# Revit family: Roof_Top_AHU-Systemair-ERV_Series
name_source: partatom
category: Mechanical Equipment
revit_build: Autodesk Revit MEP 2013 (Build: 20121003_2115(x64)
units: mm (PartAtom-declared; Revit-internal decimal feet)

## types (1)
- ERV 1300RT-EC
    Apparent Load = 0 VA
    Back Unit Width = 1' - 2 1/8"
    Bottom Opening Length 1 = 1' - 11 1/2"
    Bottom Opening Length 2 = 2' - 0 3/4"
    Bottom Opening Width 1 = 0' - 7 1/4"
    Bottom Opening Width 2 = 0' - 7"
    Description = See Part Description
    Equipment Abbreviation = AH
    Family Version = 1.0.0
    Flow (Exhaust) = 0 CFM
    Flow (Supply) = 0 CFM
    Height = 3' - 5"
    Length = 3' - 11"
    Main Unit Length = 2' - 10"
    Main Unit Width = 4' - 2"
    Manufacturer = Systemair
    Model = See Part Number
    Model Disclaimer = Contact Systemair for more information
    Product Documentation Link = http://www.systemair.com
    Product Page URL = http://www.systemair.com
    Total Pressure (Return) = 0.00 in-wg
    Total Pressure (Supply) = 0.00 in-wg
    URL = www.systemair.com
    Voltage = 0 V
    Width = 5' - 10"

## geometry (parser evidence)
native form markers: Blend x4, Sweep x1
no freeform markers — native parametric forms only
